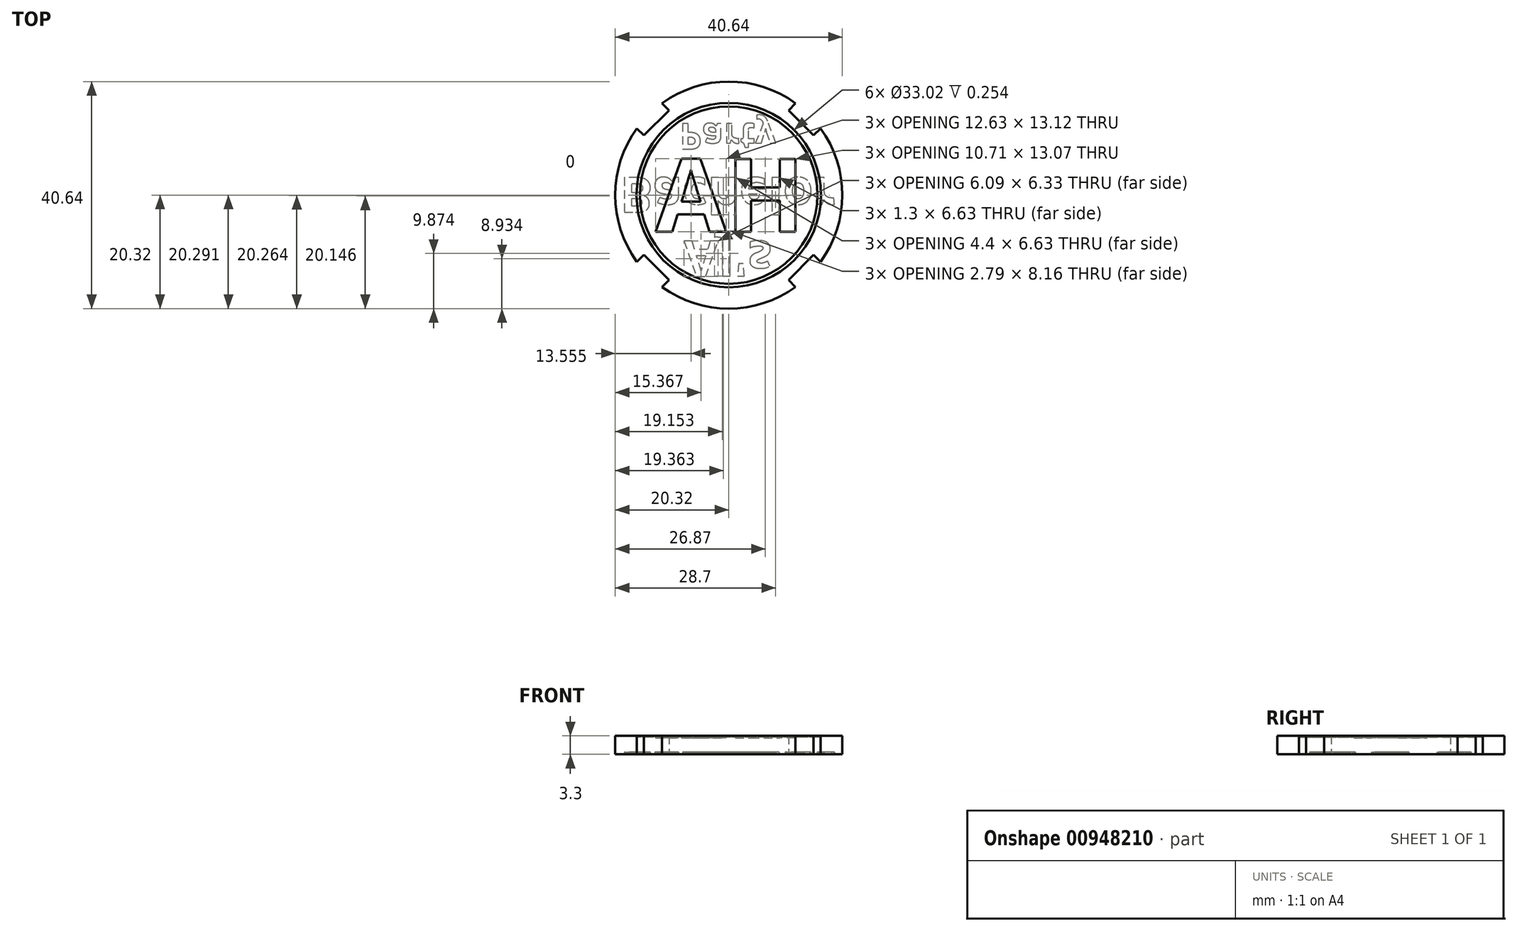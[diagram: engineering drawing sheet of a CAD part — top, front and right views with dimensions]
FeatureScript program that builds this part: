
annotation { "Feature Type Name" : "Feature", "Feature Type Description" : "" }
export const myFeature = defineFeature(function(context is Context, id is Id, definition is map)
    precondition{}
    {
        {
            var Q0;
            Q0=qCreatedBy(makeId("Top.planeOp"),FACE);
            var sketch = newSketch(context, id + "F0", { "sketchPlane" : qUnion([Q0])});
            skCircle(sketch, "E0", {"center": v(0, 0) * mm, "radius": 20.32 * mm});
            skSolve(sketch);
        }
        {
            var Q0;
            Q0=makeQuery(id+"F0.imprint","IMPRINT",FACE,{"disambiguationData":[TD([[makeQuery(id+"F0.imprint","IMPRINT",EDGE,{"derivedFrom":sQuery(id+"F0.wireOp",EDGE,"E0")}),1.0]])]});
            extrude(context, id + "F1", {"entities" : qUnion([Q0]), "depth" : 3.3 * mm, "offsetDistance" : 25.4 * mm});
        }
        {
            var Q0;
            Q0=makeQuery(id+"F1.opExtrude","CAP_FACE",FACE,{"disambiguationData":[OSD([sQuery(id+"F0.wireOp",EDGE,"E0")])],"isStart":true});
            var sketch = newSketch(context, id + "F2", { "sketchPlane" : qUnion([Q0])});
            skText(sketch, "E1", { "text": "Bachelor", "fontName": "OpenSans-Bold.ttf"});
            const initialGuessF2  = {"E1": [-0.01945, -0.00314, 1, 0, 0.00628]};
            skSetInitialGuess(sketch, initialGuessF2);
            skSolve(sketch);
        }
        {
            var Q0;
            Q0=makeQuery(id+"F2.imprint","IMPRINT",FACE,{"disambiguationData":[TD([[makeQuery(id+"F2.imprint","IMPRINT",EDGE,{"derivedFrom":sQuery(id+"F2.wireOp",EDGE,"E1.sketch_text.stroke-0")}),1.0]])]});
            var sketch = newSketch(context, id + "F3", { "sketchPlane" : qUnion([Q0])});
            skText(sketch, "E2", { "text": "AJ\'s", "fontName": "OpenSans-Bold.ttf"});
            const initialGuessF3  = {"E2": [-0.008, 0.00822, 1, 0, 0.00636]};
            skSetInitialGuess(sketch, initialGuessF3);
            skSolve(sketch);
        }
        {
            var Q0;
            Q0=makeQuery(id+"F2.imprint","IMPRINT",FACE,{"disambiguationData":[TD([[makeQuery(id+"F2.imprint","IMPRINT",EDGE,{"derivedFrom":sQuery(id+"F2.wireOp",EDGE,"E1.sketch_text.stroke-0")}),1.0]])]});
            var sketch = newSketch(context, id + "F4", { "sketchPlane" : qUnion([Q0])});
            skText(sketch, "E3", { "text": "Party", "fontName": "OpenSans-Bold.ttf"});
            const initialGuessF4  = {"E3": [-0.00883, -0.01283, 1, 0, 0.00462]};
            skSetInitialGuess(sketch, initialGuessF4);
            skSolve(sketch);
        }
        {
            var Q0;
            Q0=makeQuery(id+"F2.imprint","IMPRINT",FACE,{"disambiguationData":[TD([[makeQuery(id+"F2.imprint","IMPRINT",EDGE,{"derivedFrom":sQuery(id+"F2.wireOp",EDGE,"E1.sketch_text.stroke-0")}),1.0]])]});
            var sketch = newSketch(context, id + "F5", { "sketchPlane" : qUnion([Q0])});
            skLineSegment(sketch, "E4", {"start": v(-14.37, 14.37) * mm, "end": v(14.37, -14.37) * mm, "construction": true});
            skLineSegment(sketch, "E5", {"start": v(-15.18, 10.69) * mm, "end": v(-10.69, 15.18) * mm});
            skLineSegment(sketch, "E6", {"start": v(-10.69, 15.18) * mm, "end": v(-11.95, 16.44) * mm});
            skLineSegment(sketch, "E7", {"start": v(-15.18, 10.69) * mm, "end": v(-16.44, 11.95) * mm});
            skArc(sketch, "E8", {"start": v(-11.95, 16.44) * mm, "mid": v(-14.37, 14.37) * mm, "end": v(-16.44, 11.95) * mm});
            skLineSegment(sketch, "E9.1.0", {"start": v(-15.18, -10.69) * mm, "end": v(-16.44, -11.95) * mm});
            skArc(sketch, "E9.1.1", {"start": v(-16.44, -11.95) * mm, "mid": v(-14.37, -14.37) * mm, "end": v(-11.95, -16.44) * mm});
            skLineSegment(sketch, "E9.1.2", {"start": v(-10.69, -15.18) * mm, "end": v(-11.95, -16.44) * mm});
            skLineSegment(sketch, "E9.1.3", {"start": v(-10.69, -15.18) * mm, "end": v(-15.18, -10.69) * mm});
            skLineSegment(sketch, "E9.2.0", {"start": v(10.69, -15.18) * mm, "end": v(11.95, -16.44) * mm});
            skArc(sketch, "E9.2.1", {"start": v(11.95, -16.44) * mm, "mid": v(14.37, -14.37) * mm, "end": v(16.44, -11.95) * mm});
            skLineSegment(sketch, "E9.2.2", {"start": v(15.18, -10.69) * mm, "end": v(16.44, -11.95) * mm});
            skLineSegment(sketch, "E9.2.3", {"start": v(15.18, -10.69) * mm, "end": v(10.69, -15.18) * mm});
            skLineSegment(sketch, "E9.3.0", {"start": v(15.18, 10.69) * mm, "end": v(16.44, 11.95) * mm});
            skArc(sketch, "E9.3.1", {"start": v(16.44, 11.95) * mm, "mid": v(14.37, 14.37) * mm, "end": v(11.95, 16.44) * mm});
            skLineSegment(sketch, "E9.3.2", {"start": v(10.69, 15.18) * mm, "end": v(11.95, 16.44) * mm});
            skLineSegment(sketch, "E9.3.3", {"start": v(10.69, 15.18) * mm, "end": v(15.18, 10.69) * mm});
            skSolve(sketch);
        }
        {
            var Q0;
            Q0 = qSketchRegion(id + "F5", true);
            extrude(context, id + "F6", {"entities" : qUnion([Q0]), "operationType" : NewBodyOperationType.REMOVE, "oppositeDirection" : true, "depth" : 3.3 * mm, "offsetDistance" : 25.4 * mm});
        }
        {
            var Q0;
            Q0=makeQuery(id+"F1.opExtrude","CAP_FACE",FACE,{"disambiguationData":[OSD([sQuery(id+"F0.wireOp",EDGE,"E0")])],"isStart":false});
            var sketch = newSketch(context, id + "F7", { "sketchPlane" : qUnion([Q0])});
            skCircle(sketch, "E10", {"center": v(0, 0) * mm, "radius": 16.51 * mm});
            skCircle(sketch, "E11", {"center": v(0, 0) * mm, "radius": 15.88 * mm});
            skSolve(sketch);
        }
        {
            var Q0;
            Q0 = qSketchRegion(id + "F7", true);
            extrude(context, id + "F8", {"entities" : qUnion([Q0]), "operationType" : NewBodyOperationType.REMOVE, "oppositeDirection" : true, "depth" : 0.25 * mm, "offsetDistance" : 25.4 * mm});
        }
        {
            var Q0;
            Q0 = qSketchRegion(id + "F2", true);
            extrude(context, id + "F9", {"entities" : qUnion([Q0]), "operationType" : NewBodyOperationType.REMOVE, "oppositeDirection" : true, "depth" : 0.38 * mm, "offsetDistance" : 25.4 * mm});
        }
        {
            var Q0;
            Q0 = qSketchRegion(id + "F3", true);
            extrude(context, id + "F10", {"entities" : qUnion([Q0]), "operationType" : NewBodyOperationType.REMOVE, "oppositeDirection" : true, "depth" : 0.38 * mm, "offsetDistance" : 25.4 * mm});
        }
        {
            var Q0;
            Q0 = qSketchRegion(id + "F4", true);
            extrude(context, id + "F11", {"entities" : qUnion([Q0]), "operationType" : NewBodyOperationType.REMOVE, "oppositeDirection" : true, "depth" : 0.38 * mm, "offsetDistance" : 25.4 * mm});
        }
        {
            var Q0;
            Q0=makeQuery(id+"F8.boolean.opBoolean","SPLIT",FACE,{"disambiguationData":[TD([makeQuery(id+"F8.opExtrude","SWEPT_FACE",FACE,{"disambiguationData":[OSD([sQuery(id+"F7.wireOp",EDGE,"E11")])]})])],"derivedFrom":makeQuery(id+"F1.opExtrude","CAP_FACE",FACE,{"disambiguationData":[OSD([sQuery(id+"F0.wireOp",EDGE,"E0")])],"isStart":false})});
            var sketch = newSketch(context, id + "F12", { "sketchPlane" : qUnion([Q0])});
            skText(sketch, "E12", { "text": "AH", "fontName": "OpenSans-Bold.ttf"});
            const initialGuessF12  = {"E12": [-0.01308, -0.00659, 1, 0, 0.01318]};
            skSetInitialGuess(sketch, initialGuessF12);
            skSolve(sketch);
        }
        {
            var Q0;
            Q0 = qSketchRegion(id + "F12", true);
            extrude(context, id + "F13", {"entities" : qUnion([Q0]), "operationType" : NewBodyOperationType.REMOVE, "oppositeDirection" : true, "depth" : 0.38 * mm, "offsetDistance" : 25.4 * mm});
        }
    });
